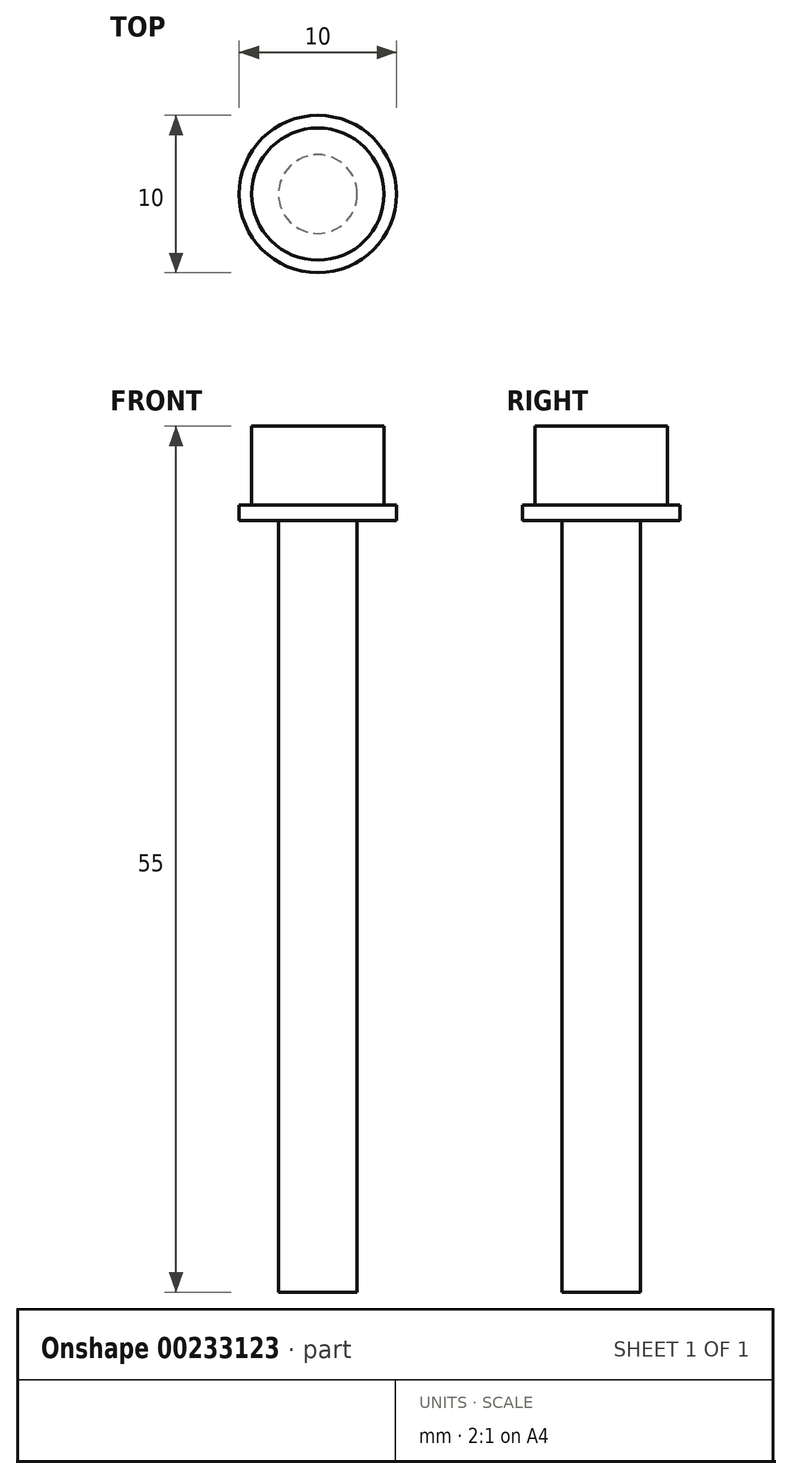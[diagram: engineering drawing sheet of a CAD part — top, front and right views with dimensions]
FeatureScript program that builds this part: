
annotation { "Feature Type Name" : "Feature", "Feature Type Description" : "" }
export const myFeature = defineFeature(function(context is Context, id is Id, definition is map)
    precondition{}
    {
        {
            var Q0;
            Q0=qCreatedBy(makeId("Top.planeOp"),FACE);
            var sketch = newSketch(context, id + "F0", { "sketchPlane" : qUnion([Q0])});
            skCircle(sketch, "E0", {"center": v(0, 0) * mm, "radius": 2.5 * mm});
            skSolve(sketch);
        }
        {
            var Q0;
            Q0=qSketchRegion(id+"F0",true);
            extrude(context, id + "F1", {"entities" : qUnion([Q0]), "oppositeDirection" : true, "offsetDistance" : 25 * mm, "depth" : 50 * mm});
        }
        {
            var Q0;
            Q0=qCreatedBy(makeId("Top.planeOp"),FACE);
            var sketch = newSketch(context, id + "F2", { "sketchPlane" : qUnion([Q0])});
            skCircle(sketch, "E1", {"center": v(0, 0) * mm, "radius": 4.2 * mm});
            skSolve(sketch);
        }
        {
            var Q0;
            Q0=qSketchRegion(id+"F2",true);
            extrude(context, id + "F3", {"entities" : qUnion([Q0]), "operationType" : NewBodyOperationType.ADD, "depth" : 5 * mm});
        }
        {
            var Q0;
            Q0=qCreatedBy(makeId("Top.planeOp"),FACE);
            var sketch = newSketch(context, id + "F4", { "sketchPlane" : qUnion([Q0])});
            skCircle(sketch, "E2", {"center": v(0, 0) * mm, "radius": 5 * mm});
            skSolve(sketch);
        }
        {
            var Q0;
            Q0=qSketchRegion(id+"F4",true);
            extrude(context, id + "F5", {"entities" : qUnion([Q0]), "operationType" : NewBodyOperationType.ADD, "oppositeDirection" : true, "depth" : 1 * mm});
        }
    });
